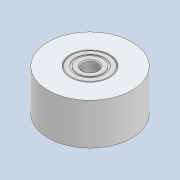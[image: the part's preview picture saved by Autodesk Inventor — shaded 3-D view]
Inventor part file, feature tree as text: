
AUTODESK INVENTOR PART (.ipt)
format: ipt  version: 2020 (Build 240168000, 168)  size: 388,096 bytes
history: native  units: in
note: dims shown in document units (in); Inventor stores cm internally (conversion verified against a paired STEP export)
features: other x4, extrude x1, sketch x1
ambient origin geometry x8: Origin, YZ Plane, XZ Plane, XY Plane, X Axis, Y Axis, Z Axis, Center Point
bodies: Solid1 (feature_tree), Solid2 (feature_tree), Solid3 (feature_tree)
feature tree (6):
  other  "16T W6 B3 Without T.iam"
  other  "16T W6 B3 Without T, Idler Pulley.ipt:1"
  other  "16T W6 B3 Without T, 693-2Z BEARING, 8 mm OD, 3 mm ID, 4 mm WIDTH_DEFAULT.ipt:1"
  other  "16T W6 B3 Without T, 693-2Z BEARING, 8 mm OD, 3 mm ID, 4 mm WIDTH_DEFAULT.ipt:2"
  extrude  "Extrusion1"  Depth=0.3937in
  sketch  "Sketch1"  dims[d0=0.3937in d1=0.6693in d2=1.0in d3=0.0in]
